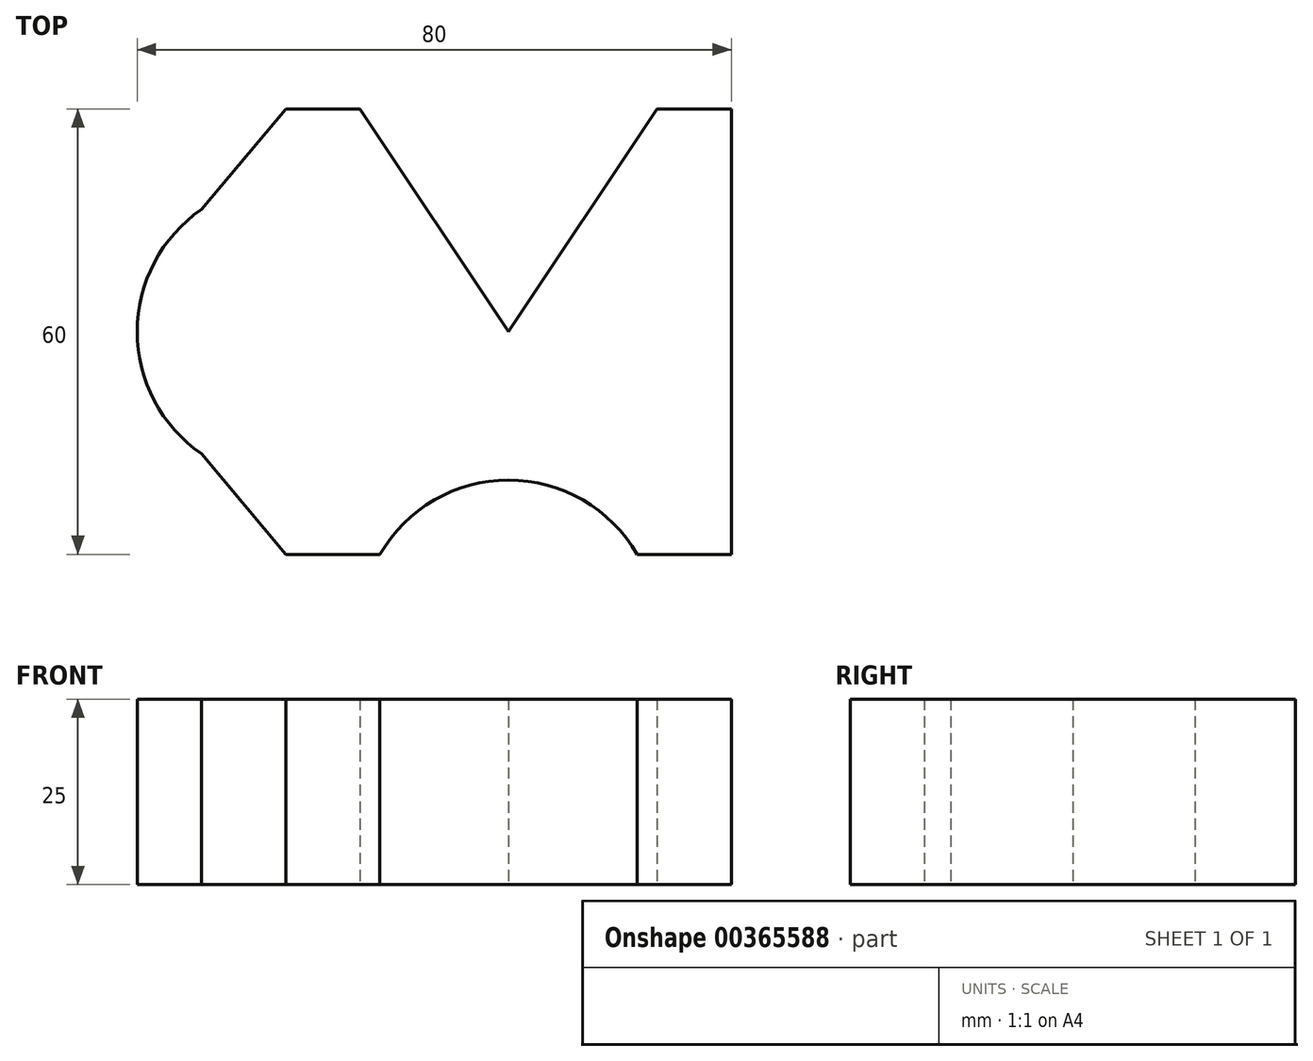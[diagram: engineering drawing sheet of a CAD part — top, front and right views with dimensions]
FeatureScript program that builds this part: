
annotation { "Feature Type Name" : "Feature", "Feature Type Description" : "" }
export const myFeature = defineFeature(function(context is Context, id is Id, definition is map)
    precondition{}
    {
        {
            var Q0;
            Q0=qCreatedBy(makeId("Top.planeOp"),FACE);
            var sketch = newSketch(context, id + "F0", { "sketchPlane" : qUnion([Q0])});
            skLineSegment(sketch, "E0", {"start": v(0, 0) * mm, "end": v(20, 30) * mm});
            skLineSegment(sketch, "E1", {"start": v(20, 30) * mm, "end": v(30, 30) * mm});
            skLineSegment(sketch, "E2", {"start": v(30, 30) * mm, "end": v(30, -30) * mm});
            skLineSegment(sketch, "E3", {"start": v(30, -30) * mm, "end": v(17.32, -30) * mm});
            skArc(sketch, "E4", {"start": v(17.32, -30) * mm, "mid": v(0, -20) * mm, "end": v(-17.32, -30) * mm});
            skLineSegment(sketch, "E5", {"start": v(-17.32, -30) * mm, "end": v(-30, -30) * mm});
            skLineSegment(sketch, "E6", {"start": v(-30, -30) * mm, "end": v(-41.36, -16.46) * mm});
            skLineSegment(sketch, "E7", {"start": v(-41.36, 16.46) * mm, "end": v(-30, 30) * mm});
            skLineSegment(sketch, "E8", {"start": v(-30, 30) * mm, "end": v(-20, 30) * mm});
            skLineSegment(sketch, "E9", {"start": v(-20, 30) * mm, "end": v(0, 0) * mm});
            skLineSegment(sketch, "E10", {"start": v(-30, 30) * mm, "end": v(-30, -46.08) * mm, "construction": true});
            skArc(sketch, "E11", {"start": v(-41.36, 16.46) * mm, "mid": v(-50, 0) * mm, "end": v(-41.36, -16.46) * mm});
            skSolve(sketch);
        }
        {
            var Q0;
            Q0 = qSketchRegion(id + "F0", true);
            extrude(context, id + "F1", {"entities" : qUnion([Q0]), "depth" : 25 * mm});
        }
    });
